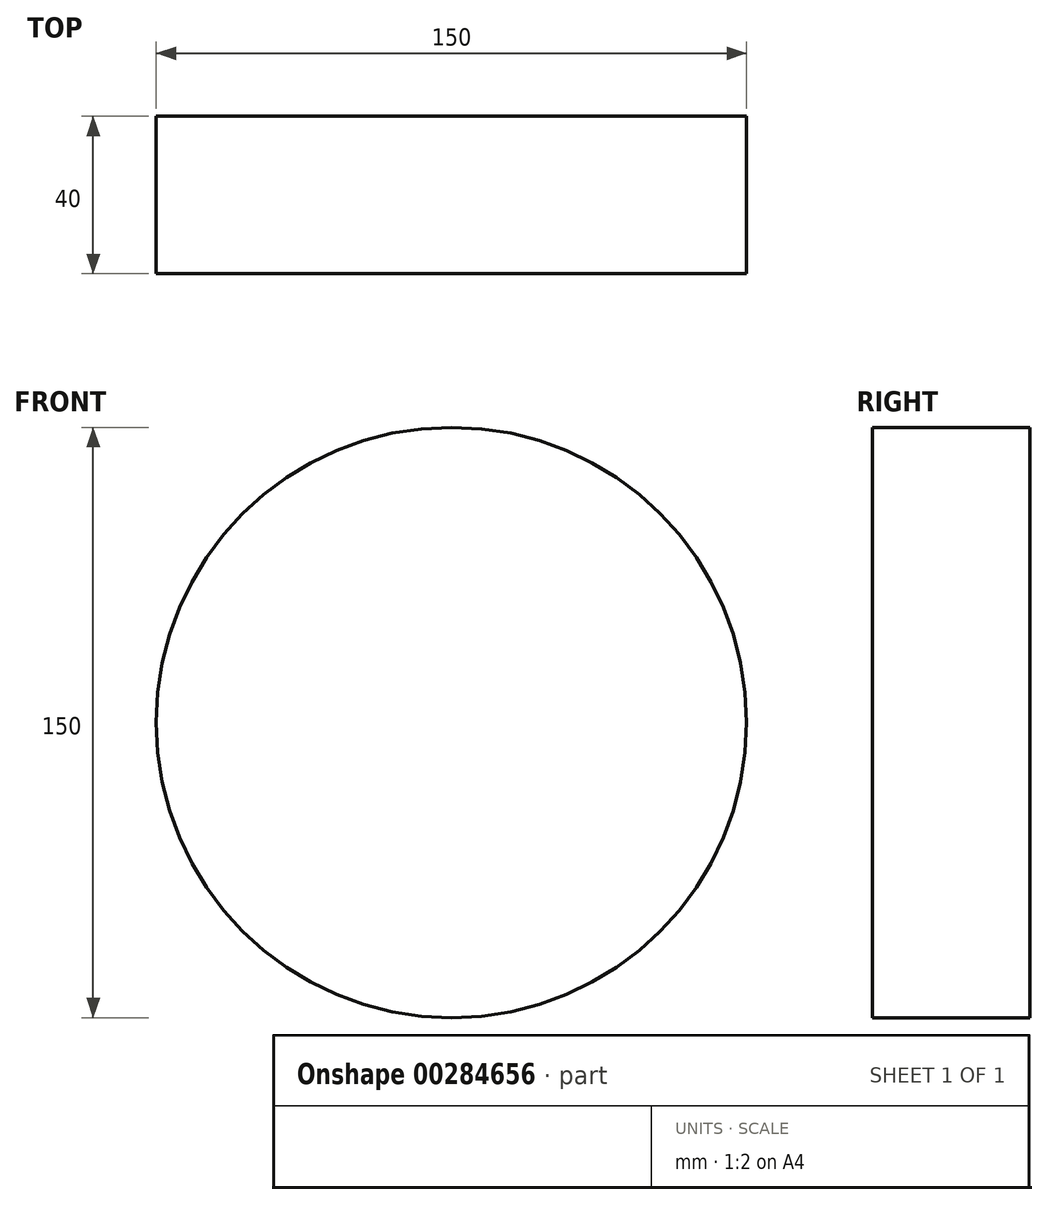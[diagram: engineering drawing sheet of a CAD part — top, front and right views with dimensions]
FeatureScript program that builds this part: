
annotation { "Feature Type Name" : "Feature", "Feature Type Description" : "" }
export const myFeature = defineFeature(function(context is Context, id is Id, definition is map)
    precondition{}
    {
        {
            var Q0;
            Q0=qCreatedBy(makeId("Front.planeOp"),FACE);
            var sketch = newSketch(context, id + "F0", { "sketchPlane" : qUnion([Q0])});
            skCircle(sketch, "E0", {"center": v(0, 0) * mm, "radius": 75 * mm});
            skSolve(sketch);
        }
        {
            var Q0;
            Q0=makeQuery(id+"F0.imprint","IMPRINT",FACE,{"disambiguationData":[TD([[makeQuery(id+"F0.imprint","IMPRINT",EDGE,{"derivedFrom":sQuery(id+"F0.wireOp",EDGE,"E0")}),1.0]])]});
            extrude(context, id + "F1", {"entities" : qUnion([Q0]), "depth" : 40 * mm});
        }
    });
